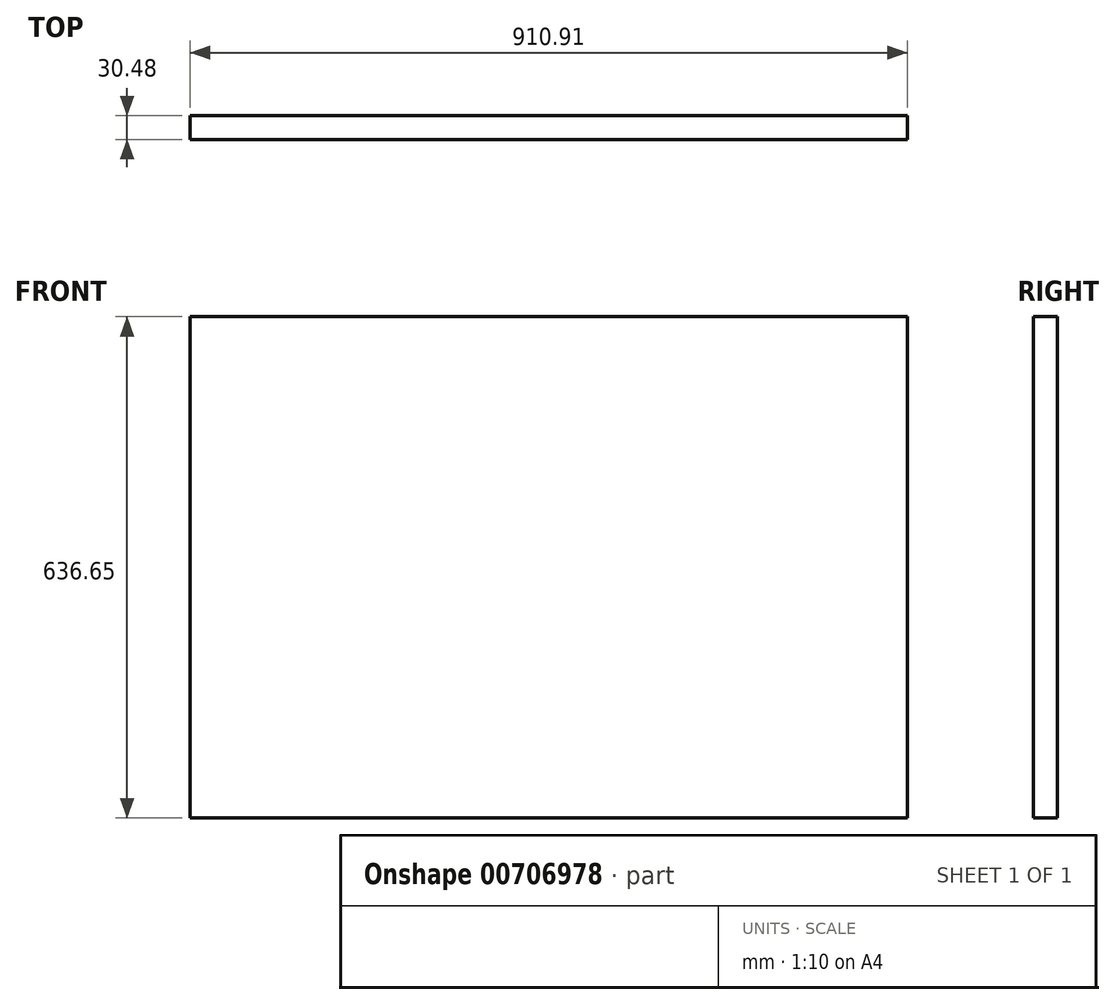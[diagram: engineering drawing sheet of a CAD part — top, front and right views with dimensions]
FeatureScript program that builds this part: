
annotation { "Feature Type Name" : "Feature", "Feature Type Description" : "" }
export const myFeature = defineFeature(function(context is Context, id is Id, definition is map)
    precondition{}
    {
        {
            var Q0;
            Q0=qCreatedBy(makeId("Front.planeOp"),FACE);
            var sketch = newSketch(context, id + "F0", { "sketchPlane" : qUnion([Q0])});
            skLineSegment(sketch, "E0.bottom", {"start": v(-58.34, 54.64) * mm, "end": v(65.63, 54.64) * mm});
            skLineSegment(sketch, "E0.top", {"start": v(-58.34, 8.85) * mm, "end": v(65.63, 8.85) * mm});
            skLineSegment(sketch, "E0.left", {"start": v(-58.34, 54.64) * mm, "end": v(-58.34, 8.85) * mm});
            skLineSegment(sketch, "E0.right", {"start": v(65.63, 54.64) * mm, "end": v(65.63, 8.85) * mm});
            skLineSegment(sketch, "E1.left", {"start": v(-58.34, 54.64) * mm, "end": v(-58.34, 54.64) * mm});
            skLineSegment(sketch, "E1.right", {"start": v(65.63, 54.64) * mm, "end": v(65.63, 54.64) * mm});
            skLineSegment(sketch, "E2.bottom", {"start": v(65.63, -60.09) * mm, "end": v(-58.34, -60.09) * mm});
            skLineSegment(sketch, "E2.top", {"start": v(65.63, 8.85) * mm, "end": v(-58.34, 8.85) * mm});
            skLineSegment(sketch, "E2.left", {"start": v(65.63, -60.09) * mm, "end": v(65.63, 8.85) * mm});
            skLineSegment(sketch, "E2.right", {"start": v(-58.34, -60.09) * mm, "end": v(-58.34, 8.85) * mm});
            skSolve(sketch);
        }
        {
            var Q0;
            Q0 = qSketchRegion(id + "F0", true);
            extrude(context, id + "F1", {"entities" : qUnion([Q0]), "depth" : 30.48 * mm, "offsetDistance" : 30.48 * mm});
        }
        {
            var Q0;
            Q0=qCreatedBy(makeId("Front.planeOp"),FACE);
            var sketch = newSketch(context, id + "F2", { "sketchPlane" : qUnion([Q0])});
            skLineSegment(sketch, "E3.bottom", {"start": v(680.61, 292.13) * mm, "end": v(-230.3, 292.13) * mm});
            skLineSegment(sketch, "E3.top", {"start": v(680.61, -344.52) * mm, "end": v(-230.3, -344.52) * mm});
            skLineSegment(sketch, "E3.left", {"start": v(680.61, 292.13) * mm, "end": v(680.61, -344.52) * mm});
            skLineSegment(sketch, "E3.right", {"start": v(-230.3, 292.13) * mm, "end": v(-230.3, -344.52) * mm});
            skSolve(sketch);
        }
        {
            var Q0;
            Q0=makeQuery(id+"F2.imprint","IMPRINT",FACE,{"disambiguationData":[TD([[makeQuery(id+"F2.imprint","IMPRINT",EDGE,{"derivedFrom":sQuery(id+"F2.wireOp",EDGE,"E3.bottom")}),1.0]])]});
            extrude(context, id + "F3", {"entities" : qUnion([Q0]), "operationType" : NewBodyOperationType.ADD, "depth" : 30.48 * mm, "offsetDistance" : 30.48 * mm});
        }
    });
